# Revit family: EN - MT 625
name_source: partatom
category: Equipement spécialisé
units: mm (PartAtom-declared; Revit-internal decimal feet)

## family parameters
Basée sur le plan de construction = Non
Cote de connecteur circulaire = Utiliser le diamètre
Couper avec des vides une fois chargée = Non
Numéro OmniClass = 23.50.30.00
Partagée = Non
Point de calcul de pièce = Non
Titre OmniClass = Materials Handling
Toujours verticalement = Oui
Type d'élément = Normal

## types (1)
- MT 625
    Average consumption (L/h) = 5.54
    CO2 emissions = 9.62
    Commentaires du type = Télescopique fixe compact
    Créé par = ATLANCAD
    Elévation par défaut = 0.00 m
    Engine norm = Stage V
    External turning radius over tyres = 2.30 m
    Fabricant = MANITOU
    Ground clearance = 0.33 m
    I.C. Engine power rating - Power (ch) = 75
    I.C. Engine power rating - Power (kW) = 55.4
    Max. capacity = 2500.00 kg
    Max. lifting height = 5.85 m
    Max. outreach = 3.40 m
    Modèle = MT 625
    Noise at driving position (LpA) in dB(A) = 76
    Noise to environment (LwA) = 104
    Overall height = 1.92 m
    Overall length to carriage = 3.83 m
    Overall width = 1.81 m
    Tilt-down angle = 117.00°
    Tilt-up angle = 12.00°
    URL = www.manitou.com
    Unladen weight (with forks) = 4800.00 kg
    Wheelbase = 3.31 m
